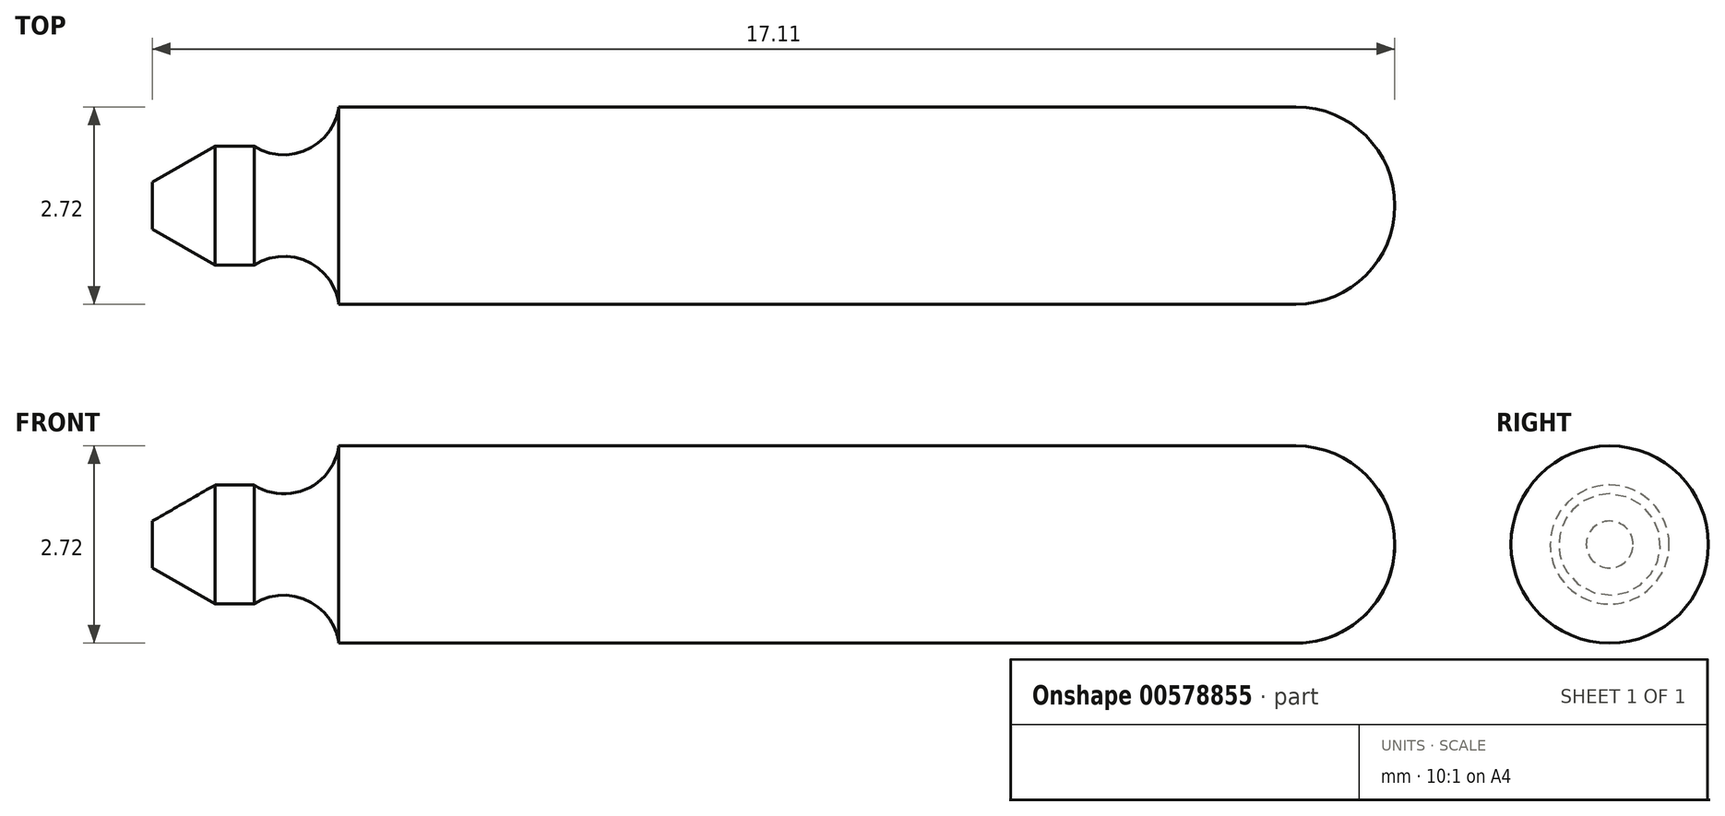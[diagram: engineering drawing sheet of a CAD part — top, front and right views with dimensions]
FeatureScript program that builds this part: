
annotation { "Feature Type Name" : "Feature", "Feature Type Description" : "" }
export const myFeature = defineFeature(function(context is Context, id is Id, definition is map)
    precondition{}
    {
        {
            var Q0;
            Q0=qCreatedBy(makeId("Right.planeOp"),FACE);
            var sketch = newSketch(context, id + "F0", { "sketchPlane" : qUnion([Q0])});
            skCircle(sketch, "E0", {"center": v(0, 0) * mm, "radius": 1.36 * mm});
            skSolve(sketch);
        }
        {
            var Q0;
            Q0=qSketchRegion(id+"F0",true);
            extrude(context, id + "F1", {"entities" : qUnion([Q0]), "depth" : 13.18 * mm});
        }
        {
            var Q0;
            Q0=qCreatedBy(makeId("Front.planeOp"),FACE);
            var sketch = newSketch(context, id + "F2", { "sketchPlane" : qUnion([Q0])});
            skLineSegment(sketch, "E1.0", {"start": v(13.18, 0) * mm, "end": v(13.18, -1.36) * mm});
            skPoint(sketch, "E2", {"position": v(13.18, 0) * mm});
            skArc(sketch, "E3", {"start": v(13.18, -1.36) * mm, "mid": v(14.14, -0.96) * mm, "end": v(14.54, 0) * mm});
            skLineSegment(sketch, "E4", {"start": v(13.18, 0) * mm, "end": v(14.54, 0) * mm});
            skPoint(sketch, "E5.orphan", {"position": v(13.18, 1.36) * mm});
            skSolve(sketch);
        }
        {
            var Q0;
            Q0=makeQuery(id+"F2.imprint","IMPRINT",FACE,{"disambiguationData":[TD([[makeQuery(id+"F2.imprint","IMPRINT",EDGE,{"derivedFrom":sQuery(id+"F2.wireOp",EDGE,"E1.0")}),1.0]])]});
            var Q1;
            Q1=sQuery(id+"F2.wireOp",EDGE,"E4");
            revolve(context, id + "F3", {"operationType" : NewBodyOperationType.ADD, "entities" : qUnion([Q0]), "axis" : qUnion([Q1]), "revolveType" : RevolveType.FULL});
        }
        {
            var Q0;
            Q0=qCreatedBy(makeId("Front.planeOp"),FACE);
            var sketch = newSketch(context, id + "F4", { "sketchPlane" : qUnion([Q0])});
            skArc(sketch, "E6", {"start": v(0, -1.36) * mm, "mid": v(-0.44, -0.77) * mm, "end": v(-1.17, -0.82) * mm});
            skLineSegment(sketch, "E7.0", {"start": v(0, 1.36) * mm, "end": v(0, -1.36) * mm});
            skPoint(sketch, "E8", {"position": v(0, 0) * mm});
            skLineSegment(sketch, "E9", {"start": v(-1.17, -0.82) * mm, "end": v(-1.7, -0.82) * mm});
            skLineSegment(sketch, "E10", {"start": v(-1.7, -0.82) * mm, "end": v(-2.57, -0.32) * mm});
            skLineSegment(sketch, "E11", {"start": v(-2.57, -0.32) * mm, "end": v(-2.57, 0) * mm});
            skLineSegment(sketch, "E12", {"start": v(-2.57, 0) * mm, "end": v(0, 0) * mm});
            skSolve(sketch);
        }
        {
            var Q0;
            {var subQ1=sQuery(id+"F4.wireOp",EDGE,"E6");Q0=makeQuery(id+"F4.imprint","IMPRINT",FACE,{"disambiguationData":[TD([[makeQuery(id+"F4.imprint","IMPRINT",EDGE,{"derivedFrom":subQ1}),-1.0]])]});}
            var Q1;
            Q1=sQuery(id+"F4.wireOp",EDGE,"E12");
            revolve(context, id + "F5", {"operationType" : NewBodyOperationType.ADD, "entities" : qUnion([Q0]), "axis" : qUnion([Q1]), "revolveType" : RevolveType.FULL});
        }
    });
